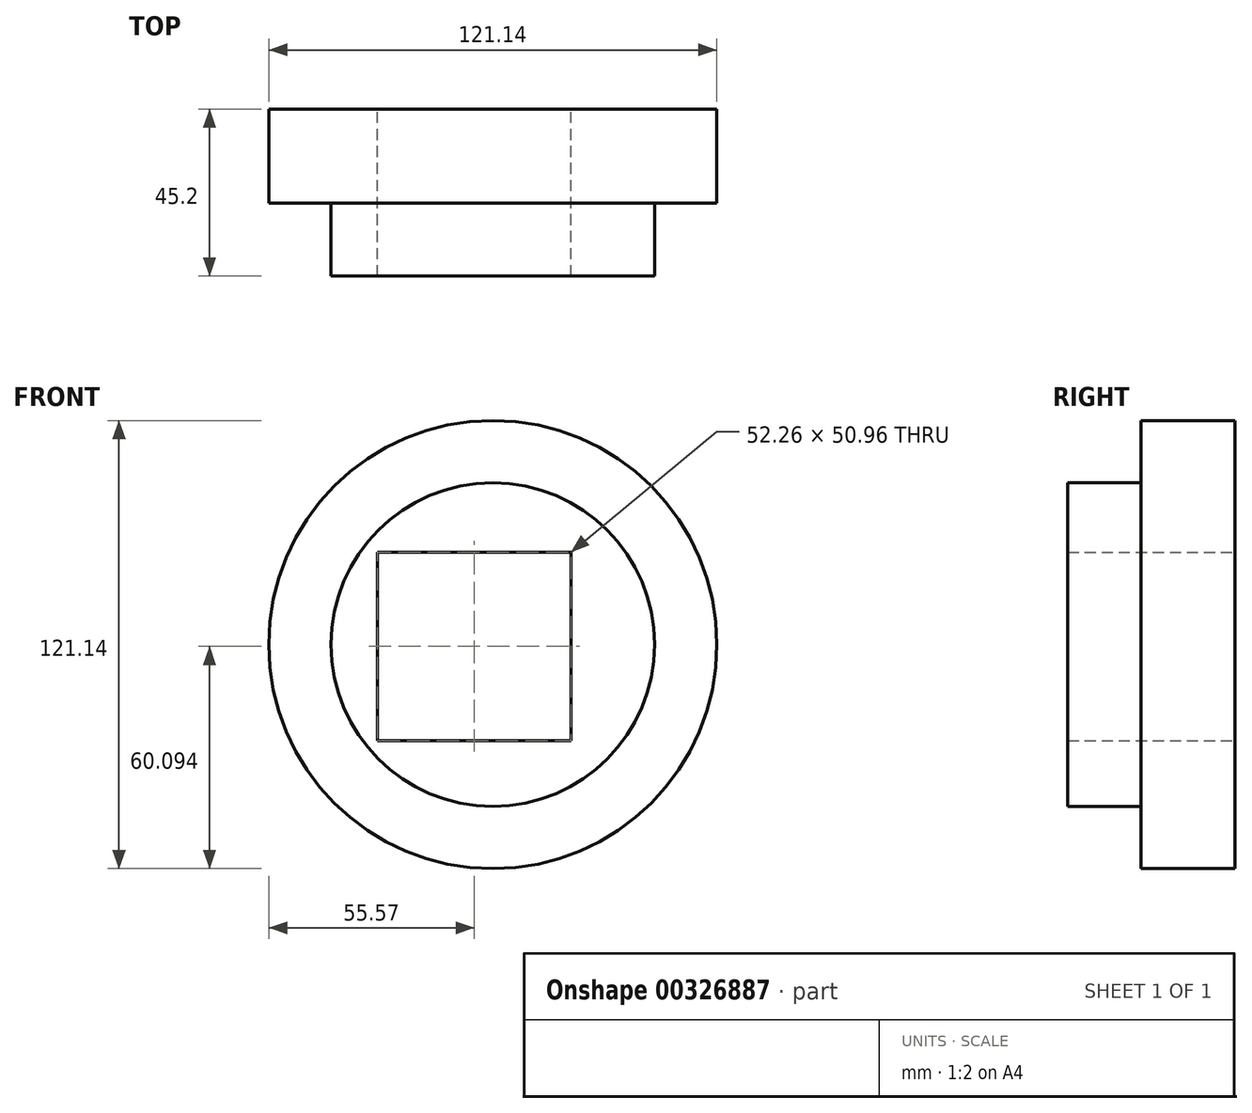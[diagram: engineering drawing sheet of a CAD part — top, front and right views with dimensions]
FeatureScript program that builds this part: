
annotation { "Feature Type Name" : "Feature", "Feature Type Description" : "" }
export const myFeature = defineFeature(function(context is Context, id is Id, definition is map)
    precondition{}
    {
        {
            var Q0;
            Q0=qCreatedBy(makeId("Front.planeOp"),FACE);
            var sketch = newSketch(context, id + "F0", { "sketchPlane" : qUnion([Q0])});
            skCircle(sketch, "E0", {"center": v(0, 0) * mm, "radius": 60.57 * mm});
            skSolve(sketch);
        }
        {
            var Q0;
            Q0=makeQuery(id+"F0.imprint","IMPRINT",FACE,{"disambiguationData":[TD([[makeQuery(id+"F0.imprint","IMPRINT",EDGE,{"derivedFrom":sQuery(id+"F0.wireOp",EDGE,"E0")}),1.0]])]});
            extrude(context, id + "F1", {"entities" : qUnion([Q0]), "depth" : 25.4 * mm});
        }
        {
            var Q0;
            Q0=makeQuery(id+"F1.opExtrude","CAP_FACE",FACE,{"disambiguationData":[OSD([sQuery(id+"F0.wireOp",EDGE,"E0")])],"isStart":false});
            var sketch = newSketch(context, id + "F2", { "sketchPlane" : qUnion([Q0])});
            skCircle(sketch, "E1", {"center": v(0, 0) * mm, "radius": 43.73 * mm});
            skSolve(sketch);
        }
        {
            var Q0;
            Q0 = qSketchRegion(id + "F2", true);
            extrude(context, id + "F3", {"entities" : qUnion([Q0]), "operationType" : NewBodyOperationType.ADD, "depth" : 19.8 * mm});
        }
        {
            var Q0;
            Q0=makeQuery(id+"F1.opExtrude","CAP_FACE",FACE,{"disambiguationData":[OSD([sQuery(id+"F0.wireOp",EDGE,"E0")])],"isStart":true});
            var sketch = newSketch(context, id + "F4", { "sketchPlane" : qUnion([Q0])});
            skLineSegment(sketch, "E2.bottom", {"start": v(31.13, 25) * mm, "end": v(-21.13, 25) * mm});
            skLineSegment(sketch, "E2.top", {"start": v(31.13, -25.95) * mm, "end": v(-21.13, -25.95) * mm});
            skLineSegment(sketch, "E2.left", {"start": v(31.13, 25) * mm, "end": v(31.13, -25.95) * mm});
            skLineSegment(sketch, "E2.right", {"start": v(-21.13, 25) * mm, "end": v(-21.13, -25.95) * mm});
            skPoint(sketch, "E2.middle", {"position": v(5, -0.48) * mm});
            skSolve(sketch);
        }
        {
            var Q0;
            Q0=makeQuery(id+"F4.imprint","IMPRINT",FACE,{"disambiguationData":[TD([[makeQuery(id+"F4.imprint","IMPRINT",EDGE,{"derivedFrom":sQuery(id+"F4.wireOp",EDGE,"E2.bottom")}),1.0]])]});
            extrude(context, id + "F5", {"entities" : qUnion([Q0]), "operationType" : NewBodyOperationType.REMOVE, "oppositeDirection" : true, "depth" : 118.06 * mm});
        }
    });
